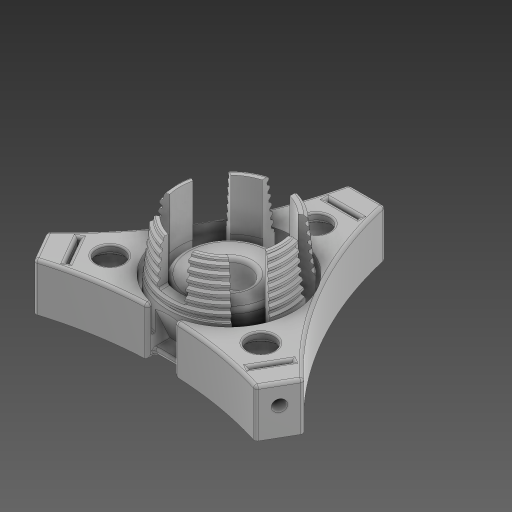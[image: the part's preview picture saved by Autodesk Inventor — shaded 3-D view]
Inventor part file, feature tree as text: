
AUTODESK INVENTOR PART (.ipt)
format: ipt  version: 2024 (Build 280153000, 153)  size: 1,766,400 bytes
history: native  units: mm
features: sketch x18, extrude x13, fillet x10, chamfer x4, hole x3, pattern_circular x3, draft x2, helix x2, plane x2, projected_geometry x2
ambient origin geometry x8: Origin, YZ Plane, XZ Plane, XY Plane, X Axis, Y Axis, Z Axis, Center Point
bodies: Solid1 (feature_tree)
feature tree (59):
  extrude  "Extrusion1"  Depth=29.5mm
  draft  "FaceDraft1"
  sketch  "Sketch2"  dims[d7=6.806784mm d8=0.55605mm]
  helix  "Coil1"  [1 undecoded]
  helix  "Coil2"  [1 undecoded]
  extrude  "Extrusion2"  Depth=0.55605mm
  extrude  "Extrusion3"  TaperAngle=0.0deg  [1 undecoded]
  fillet  "Fillet1"  [1 undecoded]
  chamfer  "Chamfer1"  Distance=0.3mm Angle=45.0deg
  plane  "Work Plane1"
  extrude  "Extrusion4"  TaperAngle=0.0deg  [1 undecoded]
  extrude  "Extrusion8"  Depth=60.0mm TaperAngle=360.0deg
  hole  "Hole2"  [1 undecoded]
  sketch  "Sketch13"  dims[d58=6.0mm d65=60.0mm d67=360.0deg]
  extrude  "Extrusion11"  Depth=10.0mm TaperAngle=0.0deg
  hole  "Bearing Hole"  [1 undecoded]
  pattern_circular  "Circular Pattern4"  Count=3 Angle=360.0deg
  extrude  "Extrusion13"  Depth=7.0mm TaperAngle=0.0deg
  sketch  "Sketch20"  dims[d126=6.704mm d127=6.0mm d128=9.879mm d129=8.89mm d130=90.0deg d131=8.0mm d132=20.594885mm d133=22.0mm d134=30.0mm d135=360.0deg]
  extrude  "Extrusion14"  Depth=1.55mm TaperAngle=45.0deg
  sketch  "Sketch18"  dims[d124=34.0mm]
  fillet  "Fillet9"  Radius=0.24mm
  chamfer  "Chamfer4"  [1 undecoded]
  chamfer  "Chamfer5"  Distance=2.0mm
  fillet  "Fillet11"  Radius=34.767mm
  draft  "FaceDraft2"
  fillet  "Fillet13"  Radius=9.0mm
  extrude  "Extrusion15"  TaperAngle=30.0deg  [1 undecoded]
  hole  "Hole5"  [1 undecoded]
  pattern_circular  "Circular Pattern5"  [2 undecoded]
  plane  "Work Plane4"
  extrude  "Extrusion16"  Depth=0.75mm TaperAngle=360.0deg
  fillet  "Fillet14"  Radius=16.0mm
  fillet  "Fillet16"  [1 undecoded]
  extrude  "Extrusion17"  Depth=0.75mm
  extrude  "Extrusion19"  Depth=0.75mm
  fillet  "Fillet17"  Radius=25.0mm
  fillet  "Fillet18"  Radius=22.0mm
  fillet  "Fillet19"  Radius=31.0mm
  extrude  "Extrusion20"  Depth=0.75mm TaperAngle=0.0deg
  fillet  "Fillet20"  Radius=32.8mm
  chamfer  "Chamfer6"  Distance=9.0mm
  pattern_circular  "Circular Pattern6"  [2 undecoded]
  sketch  "Sketch1"  dims[d0=24.7mm d1=29.5mm d2=12.875mm d3=0.0mm d4=1.047198mm]
  projected_geometry  "Projected Loop1"
  sketch  "Sketch3"  dims[d9=6.806784mm]
  sketch  "Sketch4"  dims[d10=2.0mm d11=10.0mm d12=70.0mm d13=-1.047198mm d14=90.0deg d15=90.0deg d16=0.0mm d17=0.0mm d18=0.6mm]
  sketch  "Sketch5"  dims[d19=2.0mm d20=10.0mm d21=10.0mm d22=1.047198mm d23=90.0deg d24=90.0deg d25=0.0mm d26=0.0mm d27=0.0mm d28=0.0mm d29=0.0mm d30=0.0mm]
  sketch  "Sketch10"  dims[d31=0.6mm d32=0.3mm d33=2.0mm d34=45.0deg]
  sketch  "Sketch11"  dims[d36=-2.0mm d42=0.0mm d43=0.0mm]
  sketch  "Sketch15"  dims[d91=33.0mm d92=12.0mm d93=0.0mm]
  sketch  "Sketch17"  dims[d94=5.3mm d95=6.0mm d96=10.0mm d97=7.0mm d98=90.0deg d99=8.0mm d100=20.594885mm d122=10.0mm d123=0.0mm]
  sketch  "Sketch21"  dims[d146=11.34464mm d147=7.0mm d148=0.0mm]
  sketch  "Sketch22"  dims[d150=1.0mm d151=1.55mm d152=2.0mm d153=45.0deg]
  sketch  "Sketch25"  dims[d154=0.5mm d155=2.0mm d156=45.0deg d158=0.24mm]
  sketch  "Sketch26"  dims[d160=1.25mm d161=0.0mm d162=0.0mm]
  sketch  "Sketch28"  dims[d163=30.0deg]
  sketch  "Sketch29"  dims[d164=0.5mm d165=2.0mm d166=34.767mm d167=9.0mm d168=30.0deg d169=7.0mm d170=0.0mm d171=3.0mm d172=6.0mm d173=9.779mm d174=7.62mm d175=90.0deg d176=7.0mm d177=0.0mm d178=5.0mm d179=30.0mm d180=360.0deg d182=16.0mm d183=0.0mm d184=0.0mm d185=0.75mm d187=0.4mm d188=25.0mm d189=22.0mm d190=31.0mm d191=7.0mm d192=0.0mm d193=32.8mm d208=9.0mm d209=0.0mm d210=1.0mm d211=0.25mm d212=0.5mm d213=7.0mm d214=60.0mm d216=360.0deg d218=8.0mm d219=6.0mm d220=0.6mm d221=0.3mm d222=0.0mm d223=0.0mm d224=0.75mm d225=0.75mm d226=2.0mm d227=45.0deg d228=30.0mm d229=360.0deg]
  projected_geometry  "Project Cut Edges3"
note: 15 required parameter values undecoded (feature->parameter linkage not recoverable at this tier; creation-order binding heuristic only, values carry confidence <= 0.55)
